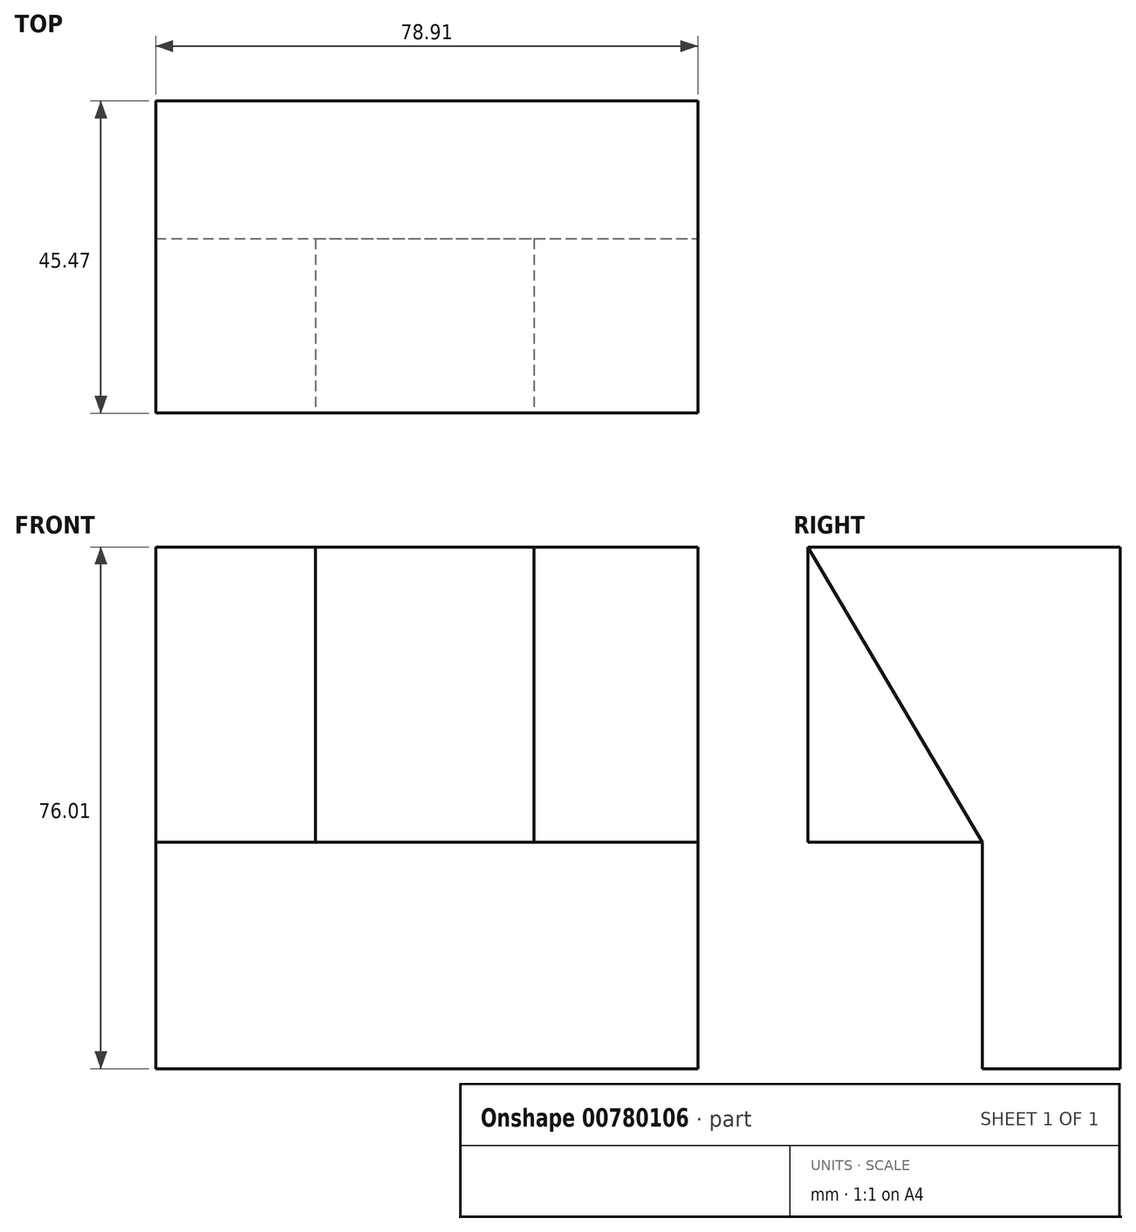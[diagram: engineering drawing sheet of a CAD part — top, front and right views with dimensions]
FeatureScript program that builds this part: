
annotation { "Feature Type Name" : "Feature", "Feature Type Description" : "" }
export const myFeature = defineFeature(function(context is Context, id is Id, definition is map)
    precondition{}
    {
        {
            var Q0;
            Q0=qCreatedBy(makeId("Front.planeOp"),FACE);
            var sketch = newSketch(context, id + "F0", { "sketchPlane" : qUnion([Q0])});
            skLineSegment(sketch, "E0", {"start": v(-38.56, 0) * mm, "end": v(40.35, 0) * mm});
            skLineSegment(sketch, "E1", {"start": v(-38.56, 0) * mm, "end": v(-38.56, 76.01) * mm});
            skLineSegment(sketch, "E2", {"start": v(40.35, 0) * mm, "end": v(40.35, 76.01) * mm});
            skLineSegment(sketch, "E3", {"start": v(-38.56, 76.01) * mm, "end": v(40.35, 76.01) * mm});
            skLineSegment(sketch, "E4", {"start": v(-38.56, 32.97) * mm, "end": v(40.35, 32.97) * mm});
            skLineSegment(sketch, "E5", {"start": v(-15.28, 76.01) * mm, "end": v(-15.28, 32.97) * mm});
            skLineSegment(sketch, "E6", {"start": v(16.52, 76.01) * mm, "end": v(16.52, 32.97) * mm});
            skSolve(sketch);
        }
        {
            var Q0;
            {var subQ0=sQuery(id+"F0.wireOp",EDGE,"E0");Q0=makeQuery(id+"F0.imprint","IMPRINT",FACE,{"disambiguationData":[TD([[makeQuery(id+"F0.imprint","IMPRINT",EDGE,{"derivedFrom":subQ0}),1.0]])]});}
            extrude(context, id + "F1", {"entities" : qUnion([Q0]), "depth" : 20.07 * mm, "offsetDistance" : 25.4 * mm});
        }
        {
            var Q0;
            {var subQ5=sQuery(id+"F0.wireOp",EDGE,"E5");Q0=makeQuery(id+"F0.imprint","IMPRINT",FACE,{"disambiguationData":[TD([[makeQuery(id+"F0.imprint","IMPRINT",EDGE,{"derivedFrom":subQ5}),-1.0]])]});}
            var Q1;
            {var subQ5=sQuery(id+"F0.wireOp",EDGE,"E6");Q1=makeQuery(id+"F0.imprint","IMPRINT",FACE,{"disambiguationData":[TD([[makeQuery(id+"F0.imprint","IMPRINT",EDGE,{"derivedFrom":subQ5}),1.0]])]});}
            extrude(context, id + "F2", {"entities" : qUnion([Q0, Q1]), "operationType" : NewBodyOperationType.ADD, "depth" : 45.47 * mm, "offsetDistance" : 25.4 * mm});
        }
        {
            var Q0;
            {var subQ0=sQuery(id+"F0.wireOp",EDGE,"E1");Q0=makeQuery(id+"F2.boolean.opBoolean","MERGE",FACE,{"derivedFrom":[makeQuery(id+"F1.opExtrude","SWEPT_FACE",FACE,{"disambiguationData":[OSD([subQ0])]}),makeQuery(id+"F2.opExtrude","SWEPT_FACE",FACE,{"disambiguationData":[OSD([subQ0])]})]});}
            var sketch = newSketch(context, id + "F3", { "sketchPlane" : qUnion([Q0])});
            skLineSegment(sketch, "E7", {"start": v(45.47, 76.01) * mm, "end": v(20.07, 32.97) * mm});
            skSolve(sketch);
        }
        {
            var Q0;
            Q0=makeQuery(id+"F3.imprint","IMPRINT",FACE,{"disambiguationData":[TD([[makeQuery(id+"F3.imprint","IMPRINT",EDGE,{"derivedFrom":sQuery(id+"F3.wireOp",EDGE,"E7")}),1.0]])]});
            extrude(context, id + "F4", {"entities" : qUnion([Q0]), "operationType" : NewBodyOperationType.REMOVE, "endBound" : BoundingType.THROUGH_ALL, "oppositeDirection" : true, "depth" : 25.4 * mm, "offsetDistance" : 25.4 * mm});
        }
        {
            var Q0;
            {var subQ0=sQuery(id+"F0.wireOp",EDGE,"E5");Q0=makeQuery(id+"F0.imprint","IMPRINT",FACE,{"disambiguationData":[TD([[makeQuery(id+"F0.imprint","IMPRINT",EDGE,{"derivedFrom":subQ0}),1.0]])]});}
            extrude(context, id + "F5", {"entities" : qUnion([Q0]), "operationType" : NewBodyOperationType.ADD, "depth" : 45.47 * mm, "offsetDistance" : 25.4 * mm});
        }
    });
